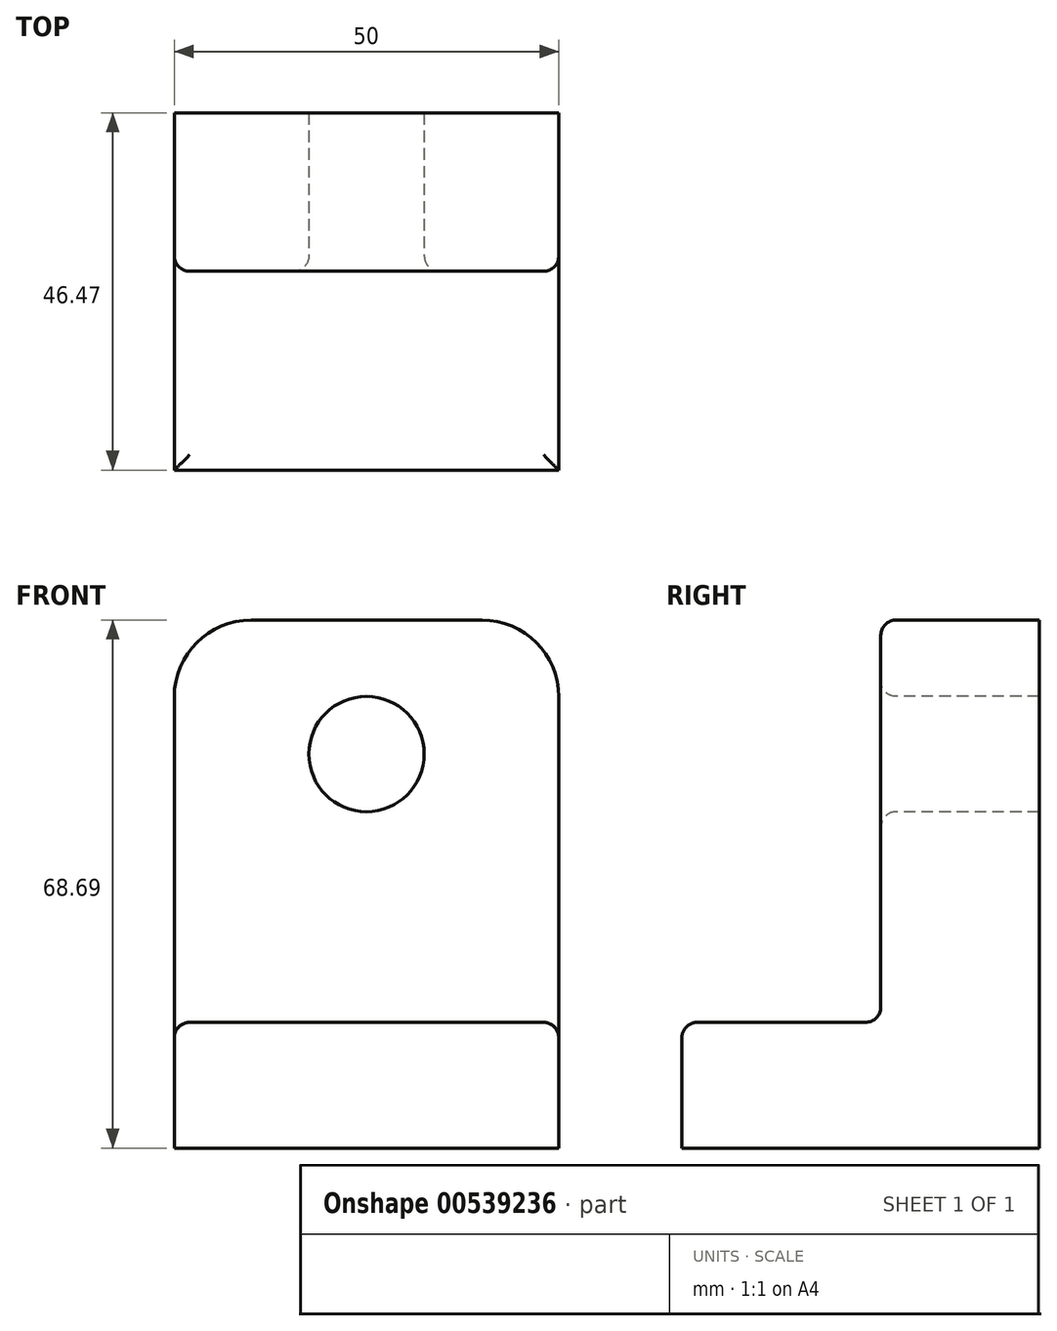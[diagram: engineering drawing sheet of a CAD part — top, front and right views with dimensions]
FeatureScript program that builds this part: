
annotation { "Feature Type Name" : "Feature", "Feature Type Description" : "" }
export const myFeature = defineFeature(function(context is Context, id is Id, definition is map)
    precondition{}
    {
        {
            var Q0;
            Q0=qCreatedBy(makeId("Right.planeOp"),FACE);
            var sketch = newSketch(context, id + "F0", { "sketchPlane" : qUnion([Q0])});
            skLineSegment(sketch, "E0", {"start": v(0, 0) * mm, "end": v(0, 68.7) * mm});
            skLineSegment(sketch, "E1", {"start": v(0, 68.7) * mm, "end": v(-20.6, 68.7) * mm});
            skLineSegment(sketch, "E2", {"start": v(-20.6, 68.7) * mm, "end": v(-20.6, 16.35) * mm});
            skLineSegment(sketch, "E3", {"start": v(-20.6, 16.35) * mm, "end": v(-46.47, 16.35) * mm});
            skLineSegment(sketch, "E4", {"start": v(-46.47, 16.35) * mm, "end": v(-46.47, 0) * mm});
            skLineSegment(sketch, "E5", {"start": v(-46.47, 0) * mm, "end": v(0, 0) * mm});
            skSolve(sketch);
        }
        {
            var Q0;
            Q0=makeQuery(id+"F0.imprint","IMPRINT",FACE,{"disambiguationData":[TD([[makeQuery(id+"F0.imprint","IMPRINT",EDGE,{"derivedFrom":sQuery(id+"F0.wireOp",EDGE,"E0")}),1.0]])]});
            extrude(context, id + "F1", {"entities" : qUnion([Q0]), "depth" : 25 * mm, "offsetDistance" : 25 * mm});
        }
        {
            var Q0;
            Q0=makeQuery(id+"F1.opExtrude","CAP_FACE",FACE,{"disambiguationData":[OSD([sQuery(id+"F0.wireOp",EDGE,"E0"),sQuery(id+"F0.wireOp",EDGE,"E1"),sQuery(id+"F0.wireOp",EDGE,"E2"),sQuery(id+"F0.wireOp",EDGE,"E3"),sQuery(id+"F0.wireOp",EDGE,"E4"),sQuery(id+"F0.wireOp",EDGE,"E5")])],"isStart":true});
            extrude(context, id + "F2", {"entities" : qUnion([Q0]), "operationType" : NewBodyOperationType.ADD, "depth" : 25 * mm, "offsetDistance" : 25 * mm});
        }
        {
            var Q0;
            {var subQ0=sQuery(id+"F0.wireOp",EDGE,"E2");Q0=makeQuery(id+"F2.boolean.opBoolean","MERGE",FACE,{"derivedFrom":[makeQuery(id+"F1.opExtrude","SWEPT_FACE",FACE,{"disambiguationData":[OSD([subQ0])]}),makeQuery(id+"F2.opExtrude","SWEPT_FACE",FACE,{"disambiguationData":[OSD([subQ0])]})]});}
            var sketch = newSketch(context, id + "F3", { "sketchPlane" : qUnion([Q0])});
            skCircle(sketch, "E6", {"center": v(0, 51.26) * mm, "radius": 4.65 * mm});
            skSolve(sketch);
        }
        {
            var Q0;
            Q0=sQuery(id+"F3.wireOp",VERTEX,"E6.center");
            var Q1;
            Q1=makeQuery(id+"F1.opExtrude","SWEPT_BODY",BODY,{"disambiguationData":[OSD([sQuery(id+"F0.wireOp",EDGE,"E0"),sQuery(id+"F0.wireOp",EDGE,"E1"),sQuery(id+"F0.wireOp",EDGE,"E2"),sQuery(id+"F0.wireOp",EDGE,"E3"),sQuery(id+"F0.wireOp",EDGE,"E4"),sQuery(id+"F0.wireOp",EDGE,"E5")])]});
            hole(context, id + "F4", {"style" : HoleStyle.SIMPLE, "endStyle" : HoleEndStyle.THROUGH, "holeDiameter" : 15 * mm, "isTappedThrough" : true, "tappedDepth" : 12 * mm, "tapClearance" : 3, "locations" : qUnion([Q0]), "scope" : qUnion([Q1])});
        }
        {
            var Q0;
            {var subQ0=sQuery(id+"F0.wireOp",EDGE,"E2");Q0=makeQuery(id+"F2.boolean.opBoolean","MERGE",FACE,{"derivedFrom":[makeQuery(id+"F1.opExtrude","SWEPT_FACE",FACE,{"disambiguationData":[OSD([subQ0])]}),makeQuery(id+"F2.opExtrude","SWEPT_FACE",FACE,{"disambiguationData":[OSD([subQ0])]})]});}
            var Q1;
            {var subQ0=sQuery(id+"F0.wireOp",EDGE,"E3");Q1=makeQuery(id+"F2.boolean.opBoolean","MERGE",FACE,{"derivedFrom":[makeQuery(id+"F1.opExtrude","SWEPT_FACE",FACE,{"disambiguationData":[OSD([subQ0])]}),makeQuery(id+"F2.opExtrude","SWEPT_FACE",FACE,{"disambiguationData":[OSD([subQ0])]})]});}
            fillet(context, id + "F5", {"entities" : qUnion([Q0, Q1]), "radius" : 2 * mm, "tangentPropagation" : true, "allowEdgeOverflow" : false});
        }
        {
            var Q0;
            Q0=makeQuery(id+"F2.opExtrude","CAP_EDGE",EDGE,{"disambiguationData":[OSD([sQuery(id+"F0.wireOp",EDGE,"E1")])],"isStart":false});
            var Q1;
            Q1=makeQuery(id+"F1.opExtrude","CAP_EDGE",EDGE,{"disambiguationData":[OSD([sQuery(id+"F0.wireOp",EDGE,"E1")])],"isStart":false});
            fillet(context, id + "F6", {"entities" : qUnion([Q0, Q1]), "radius" : 10 * mm, "tangentPropagation" : true, "allowEdgeOverflow" : false});
        }
    });
